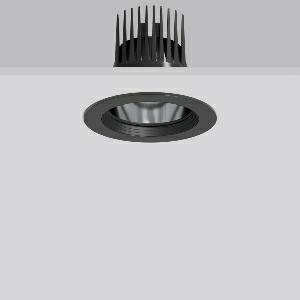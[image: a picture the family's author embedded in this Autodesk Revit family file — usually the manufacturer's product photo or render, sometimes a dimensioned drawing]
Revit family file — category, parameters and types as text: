
# Revit family: heledon_maxi_e_901780_003_76_d6dd
name_source: partatom
category: Lighting Fixtures
units: mm (PartAtom-declared; Revit-internal decimal feet)

## family parameters
Cut with Voids When Loaded = No
Host = Face
Light Source = No
Part Type = Normal
Room Calculation Point = No
Round Connector Dimension = Use Diameter
Shared = No

## types (1)
- HELEDON maxi E (1 x LED Modul 920 meat+, 2150 lm, 2000)
    Apparent Load = 33 VA
    Approval mark = CE
    CIE Flux Codes = 96 100 100 100 100
    Color Rendering = 90
    Color Temperature = 2000
    Default Elevation = 1800 mm
    Description = Series: HELEDON maxi
Round recessed downlight. Housing: die-cast aluminium, powder-coated. Black plastic ring and recessed LED to prevent glare from the side. Optical assembly with reflector made of MIRO-Silver with 98% total light reflection for outstanding efficiency - can be changed without tools. Special LED for illumination of meat included. Suitable for Recessed ceiling mounting. Installation without tools thanks to spring fastening system. Including separate LED converter with connecting cable 600 mm.High quality converter without flickering and stroboscopic effect. Through-wiring box (5 pole) available as accessory. The following accessories can be mounted without use of tools: interchangeable lenses, decorative glasses, honeycomb louvre, clear and frosted diffusers, white interchangeable plastic ring. 
Colour: deep black, matt (RAL 9005)
Diameter: 162 mm
Height: 3 mm
Cut-out diameter: 152 mm
Recess height: 200 mm
Luminaire: recess height: 135 mm
Lamp: LED
Socket: without socket
Colour temperature: meat +
System power: 33 W
Rated luminous flux: 2150 lm
Luminous efficiency: 65 lm/W
Control gear: Converter, dimmable, DALI
Protection class: II
Type of protection: IP 20
    Height = 0 mm  [stored 0 ft]
    Lamp = 1 x LED Modul 920 meat+
    Lamp Light Flux = 2150 lm
    Lamp count = 1
    Length = 162 mm
    Lifetime = 50000 h
    Luminous efficacy = 65 lm/W
    Manufacturer = RZB
    ModVariant = No
    Model = 901780.003.76
    Mounting Place = Ceiling
    Mounting Type = Recessed
    Number of Poles = 1
    OnlyDefault = Yes
    Power Factor = 1
    Product Name = HELEDON maxi E
    Product group = Recessed downlights
    ProductGroupID = 402
    Protection Class = Protection class II
    Protection Degree = IP 20
    RLX_Detail_Level = 1
    RLX_Emergency_Light_Flux = 0 lm
    RLX_Emergency_Type = 0
    RLX_Emergency_Type_DB = No
    RlxData = <blob elided: 122705 chars, md5=9780eec8>
    Socket = socket
    Standby Power = 0 W
    System Light Flux = 2150 lm
    System Power = 33 W
    Type Comments = Product without accessories
    Type Image = 901662.003.jpg
    URL = http://relux.com
    VarID = ---
    Voltage = 230 V
    Voltage Range = 220-240 V
    Weight = 0.00 kg
    Width = 0 mm  [stored 0 ft]

note: [stored X ft] marks values corroborated as IEEE doubles in the binary element streams (Revit-internal decimal feet)

## geometry (parser evidence)
native form markers: Blend x4, Sweep x12
no freeform markers — native parametric forms only
